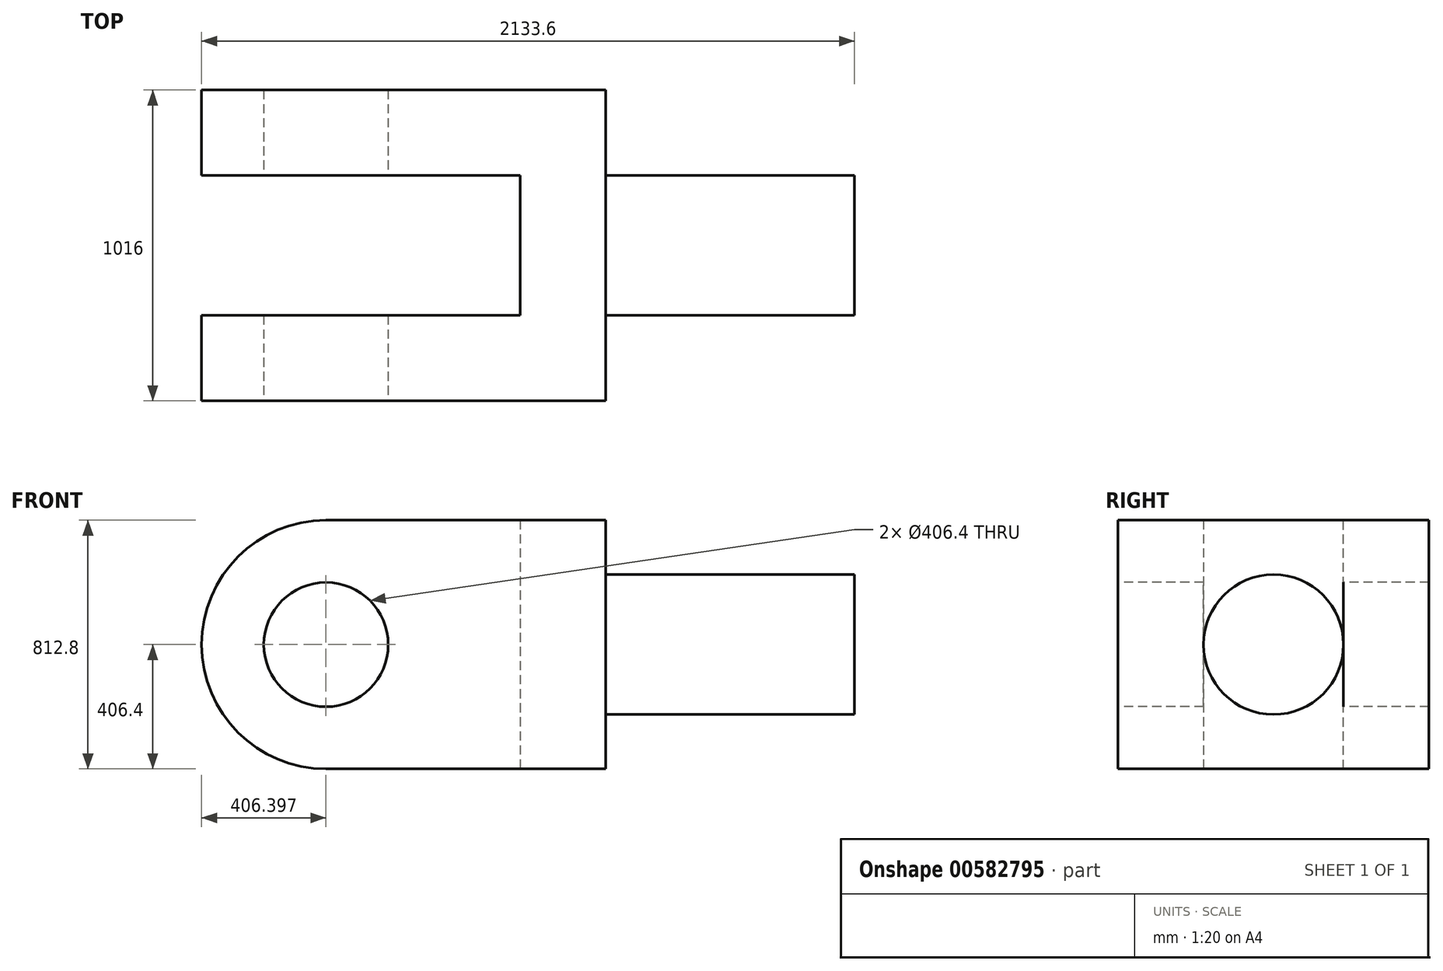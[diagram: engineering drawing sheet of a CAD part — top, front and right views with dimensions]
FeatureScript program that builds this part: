
annotation { "Feature Type Name" : "Feature", "Feature Type Description" : "" }
export const myFeature = defineFeature(function(context is Context, id is Id, definition is map)
    precondition{}
    {
        {
            var Q0;
            Q0=qCreatedBy(makeId("Top.planeOp"),FACE);
            var sketch = newSketch(context, id + "F0", { "sketchPlane" : qUnion([Q0])});
            skLineSegment(sketch, "E0", {"start": v(-69.41, -62.15) * mm, "end": v(1251.39, -62.15) * mm});
            skLineSegment(sketch, "E1", {"start": v(1251.39, -62.15) * mm, "end": v(1251.39, 953.85) * mm});
            skLineSegment(sketch, "E2", {"start": v(1251.39, 953.85) * mm, "end": v(-69.41, 953.85) * mm});
            skLineSegment(sketch, "E3", {"start": v(-69.41, 953.85) * mm, "end": v(-69.41, 674.45) * mm});
            skLineSegment(sketch, "E4", {"start": v(-69.41, 674.45) * mm, "end": v(971.99, 674.45) * mm});
            skLineSegment(sketch, "E5", {"start": v(971.99, 674.45) * mm, "end": v(971.99, 217.25) * mm});
            skLineSegment(sketch, "E6", {"start": v(971.99, 217.25) * mm, "end": v(-69.41, 217.25) * mm});
            skLineSegment(sketch, "E7", {"start": v(-69.41, 217.25) * mm, "end": v(-69.41, -62.15) * mm});
            skSolve(sketch);
        }
        {
            var Q0;
            Q0=makeQuery(id+"F0.imprint","IMPRINT",FACE,{"disambiguationData":[TD([[makeQuery(id+"F0.imprint","IMPRINT",EDGE,{"derivedFrom":sQuery(id+"F0.wireOp",EDGE,"E0")}),1.0]])]});
            extrude(context, id + "F1", {"entities" : qUnion([Q0]), "depth" : 812.8 * mm, "offsetDistance" : 25.4 * mm});
        }
        {
            var Q0;
            Q0=makeQuery(id+"F1.opExtrude","CAP_EDGE",EDGE,{"disambiguationData":[OSD([sQuery(id+"F0.wireOp",EDGE,"E7")])],"isStart":false});
            var Q1;
            Q1=makeQuery(id+"F1.opExtrude","CAP_EDGE",EDGE,{"disambiguationData":[OSD([sQuery(id+"F0.wireOp",EDGE,"E7")])],"isStart":true});
            var Q2;
            Q2=makeQuery(id+"F1.opExtrude","CAP_EDGE",EDGE,{"disambiguationData":[OSD([sQuery(id+"F0.wireOp",EDGE,"E3")])],"isStart":false});
            var Q3;
            Q3=makeQuery(id+"F1.opExtrude","CAP_EDGE",EDGE,{"disambiguationData":[OSD([sQuery(id+"F0.wireOp",EDGE,"E3")])],"isStart":true});
            fillet(context, id + "F2", {"entities" : qUnion([Q0, Q1, Q2, Q3]), "radius" : 406.4 * mm, "tangentPropagation" : true, "allowEdgeOverflow" : false});
        }
        {
            var Q0;
            Q0=makeQuery(id+"F1.opExtrude","SWEPT_FACE",FACE,{"disambiguationData":[OSD([sQuery(id+"F0.wireOp",EDGE,"E0")])]});
            var sketch = newSketch(context, id + "F3", { "sketchPlane" : qUnion([Q0])});
            skCircle(sketch, "E8", {"center": v(336.99, 406.4) * mm, "radius": 203.2 * mm});
            skSolve(sketch);
        }
        {
            var Q0;
            Q0=makeQuery(id+"F3.imprint","IMPRINT",FACE,{"disambiguationData":[TD([[makeQuery(id+"F3.imprint","IMPRINT",EDGE,{"derivedFrom":sQuery(id+"F3.wireOp",EDGE,"E8")}),1.0]])]});
            extrude(context, id + "F4", {"entities" : qUnion([Q0]), "operationType" : NewBodyOperationType.REMOVE, "endBound" : BoundingType.THROUGH_ALL, "oppositeDirection" : true, "depth" : 25.4 * mm, "offsetDistance" : 25.4 * mm});
        }
        {
            var Q0;
            Q0=makeQuery(id+"F1.opExtrude","SWEPT_FACE",FACE,{"disambiguationData":[OSD([sQuery(id+"F0.wireOp",EDGE,"E1")])]});
            var sketch = newSketch(context, id + "F5", { "sketchPlane" : qUnion([Q0])});
            skLineSegment(sketch, "E9", {"start": v(445.85, 812.8) * mm, "end": v(445.85, 0) * mm});
            skCircle(sketch, "E10", {"center": v(445.85, 406.4) * mm, "radius": 228.6 * mm});
            skSolve(sketch);
        }
        {
            var Q0;
            {var subQ0=sQuery(id+"F5.wireOp",EDGE,"E10");var subQ1=sQuery(id+"F5.wireOp",EDGE,"E9");var subQ2=makeQuery(id+"F5.imprint","INTERSECT",VERTEX,{"disambiguationData":[OD(0.0)],"derivedFrom":[subQ1,subQ0]});Q0=makeQuery(id+"F5.imprint","IMPRINT",FACE,{"disambiguationData":[TD([[makeQuery(id+"F5.imprint","IMPRINT",EDGE,{"disambiguationData":[TD([[subQ2,-1.0]])],"derivedFrom":subQ1}),-1.0]])]});}
            var Q1;
            {var subQ0=sQuery(id+"F5.wireOp",EDGE,"E10");var subQ1=sQuery(id+"F5.wireOp",EDGE,"E9");var subQ2=makeQuery(id+"F5.imprint","INTERSECT",VERTEX,{"disambiguationData":[OD(0.0)],"derivedFrom":[subQ1,subQ0]});Q1=makeQuery(id+"F5.imprint","IMPRINT",FACE,{"disambiguationData":[TD([[makeQuery(id+"F5.imprint","IMPRINT",EDGE,{"disambiguationData":[TD([[subQ2,-1.0]])],"derivedFrom":subQ1}),1.0]])]});}
            extrude(context, id + "F6", {"entities" : qUnion([Q0, Q1]), "operationType" : NewBodyOperationType.ADD, "depth" : 812.8 * mm, "offsetDistance" : 25.4 * mm});
        }
    });
